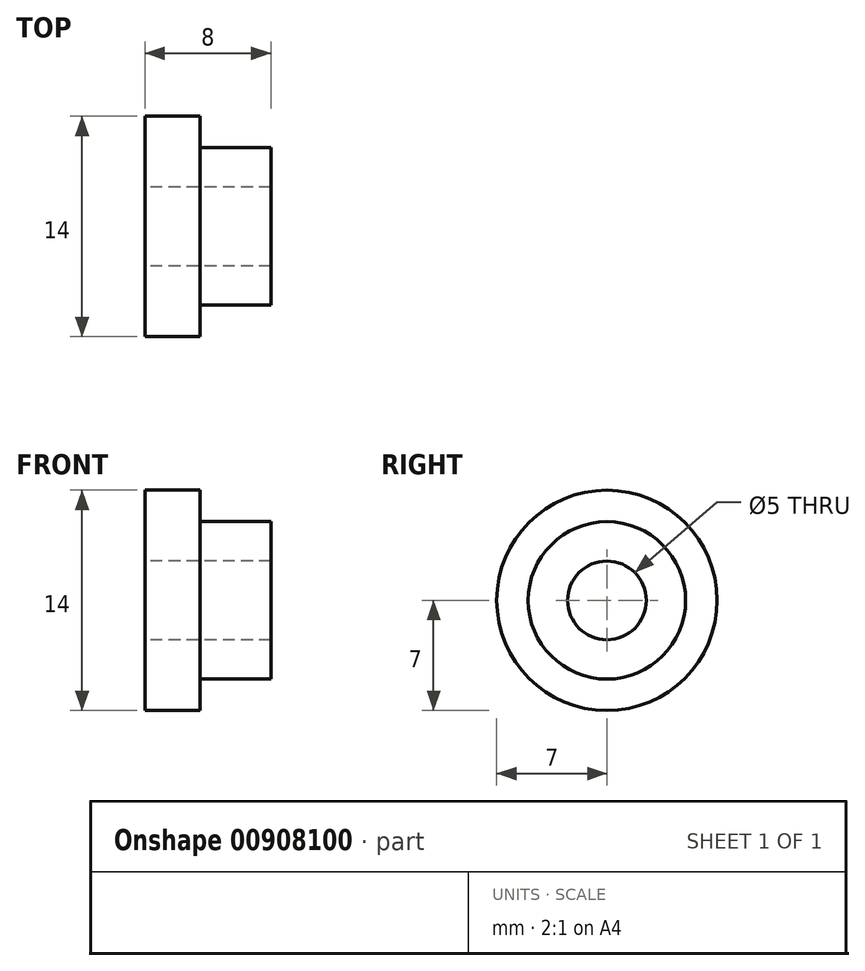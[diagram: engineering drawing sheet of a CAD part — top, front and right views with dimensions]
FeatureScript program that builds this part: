
annotation { "Feature Type Name" : "Feature", "Feature Type Description" : "" }
export const myFeature = defineFeature(function(context is Context, id is Id, definition is map)
    precondition{}
    {
        {
            var Q0;
            Q0=qCreatedBy(makeId("Front.planeOp"),FACE);
            var sketch = newSketch(context, id + "F0", { "sketchPlane" : qUnion([Q0])});
            skLineSegment(sketch, "E0.bottom", {"start": v(0, 2.5) * mm, "end": v(3.5, 2.5) * mm});
            skLineSegment(sketch, "E0.top", {"start": v(0, 7) * mm, "end": v(3.5, 7) * mm});
            skLineSegment(sketch, "E0.left", {"start": v(0, 2.5) * mm, "end": v(0, 7) * mm});
            skLineSegment(sketch, "E0.right", {"start": v(3.5, 2.5) * mm, "end": v(3.5, 7) * mm});
            skLineSegment(sketch, "E1.bottom", {"start": v(3.5, 2.5) * mm, "end": v(8, 2.5) * mm});
            skLineSegment(sketch, "E1.top", {"start": v(3.5, 5) * mm, "end": v(8, 5) * mm});
            skLineSegment(sketch, "E1.left", {"start": v(3.5, 2.5) * mm, "end": v(3.5, 5) * mm});
            skLineSegment(sketch, "E1.right", {"start": v(8, 2.5) * mm, "end": v(8, 5) * mm});
            skLineSegment(sketch, "E2.bottom", {"start": v(0, 0) * mm, "end": v(8.8, 0) * mm, "construction": true});
            skLineSegment(sketch, "E2.top", {"start": v(0, 0) * mm, "end": v(8.8, 0) * mm, "construction": true});
            skLineSegment(sketch, "E2.left", {"start": v(0, 0) * mm, "end": v(0, 0) * mm});
            skLineSegment(sketch, "E2.right", {"start": v(8.8, 0) * mm, "end": v(8.8, 0) * mm});
            skSolve(sketch);
        }
        {
            var Q0;
            Q0 = qSketchRegion(id + "F0", true);
            var Q1;
            Q1=sQuery(id+"F0.wireOp",EDGE,"E2.top");
            revolve(context, id + "F1", {"surfaceOperationType" : NewSurfaceOperationType.NEW, "entities" : qUnion([Q0]), "axis" : qUnion([Q1]), "revolveType" : RevolveType.FULL});
        }
    });
